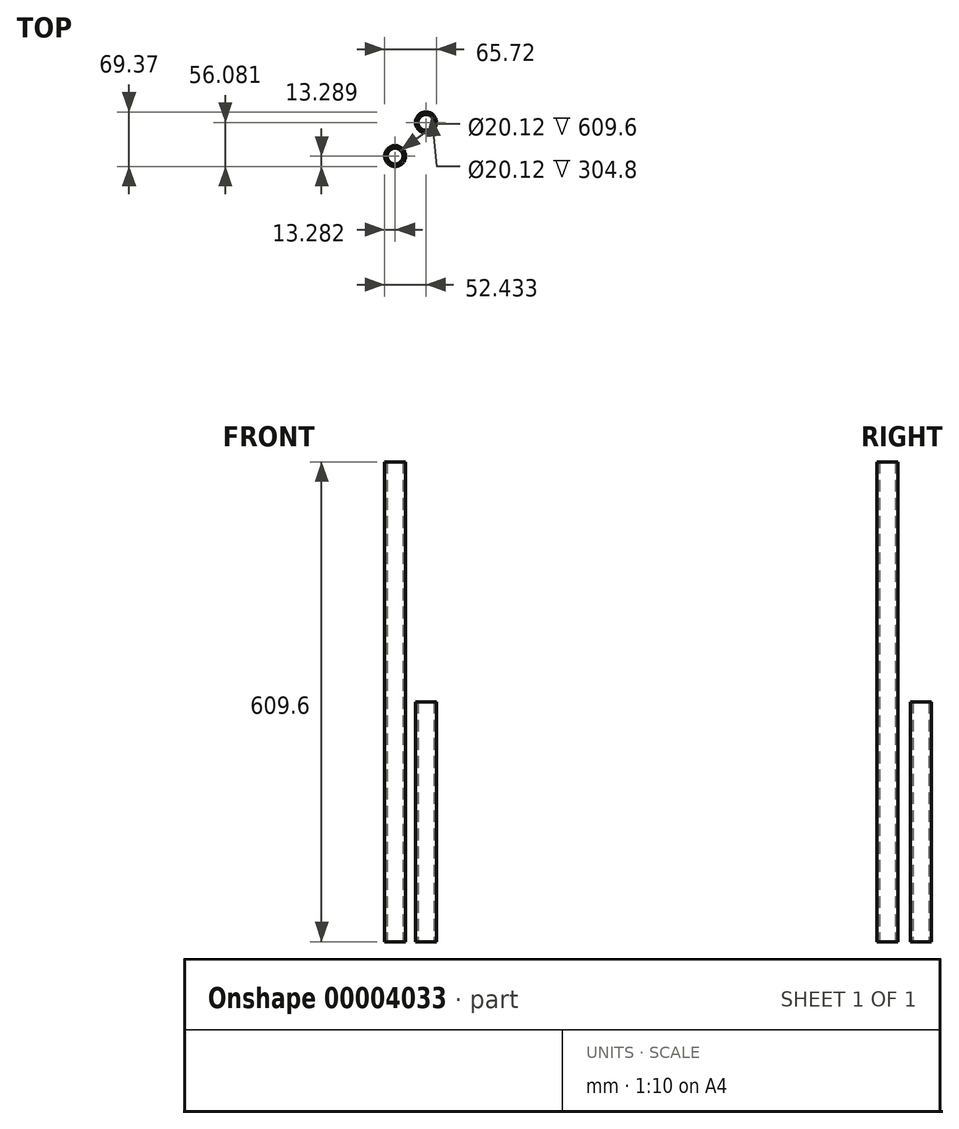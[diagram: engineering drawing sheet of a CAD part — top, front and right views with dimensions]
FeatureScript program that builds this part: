
annotation { "Feature Type Name" : "Feature", "Feature Type Description" : "" }
export const myFeature = defineFeature(function(context is Context, id is Id, definition is map)
    precondition{}
    {
        {
            var Q0;
            Q0=qCreatedBy(makeId("Top.planeOp"),FACE);
            var sketch = newSketch(context, id + "F0", { "sketchPlane" : qUnion([Q0])});
            skCircle(sketch, "E0", {"center": v(-19.2, 0.17) * mm, "radius": 13.28 * mm});
            skCircle(sketch, "E1.0", {"center": v(-19.2, 0.17) * mm, "radius": 10.06 * mm});
            skSolve(sketch);
        }
        {
            var Q0;
            Q0=makeQuery(id+"F0.imprint","IMPRINT",FACE,{"disambiguationData":[TD([[makeQuery(id+"F0.imprint","IMPRINT",EDGE,{"derivedFrom":sQuery(id+"F0.wireOp",EDGE,"E0")}),1.0]])]});
            extrude(context, id + "F1", {"entities" : qUnion([Q0]), "depth" : 304.8 * mm});
        }
        {
            var Q0;
            Q0=qCreatedBy(makeId("Top.planeOp"),FACE);
            var sketch = newSketch(context, id + "F2", { "sketchPlane" : qUnion([Q0])});
            skCircle(sketch, "E2", {"center": v(-58.36, -42.62) * mm, "radius": 13.28 * mm});
            skCircle(sketch, "E3.0", {"center": v(-58.36, -42.62) * mm, "radius": 10.06 * mm});
            skSolve(sketch);
        }
        {
            var Q0;
            Q0=makeQuery(id+"F2.imprint","IMPRINT",FACE,{"disambiguationData":[TD([[makeQuery(id+"F2.imprint","IMPRINT",EDGE,{"derivedFrom":sQuery(id+"F2.wireOp",EDGE,"E2")}),1.0]])]});
            extrude(context, id + "F3", {"entities" : qUnion([Q0]), "depth" : 609.6 * mm});
        }
    });
